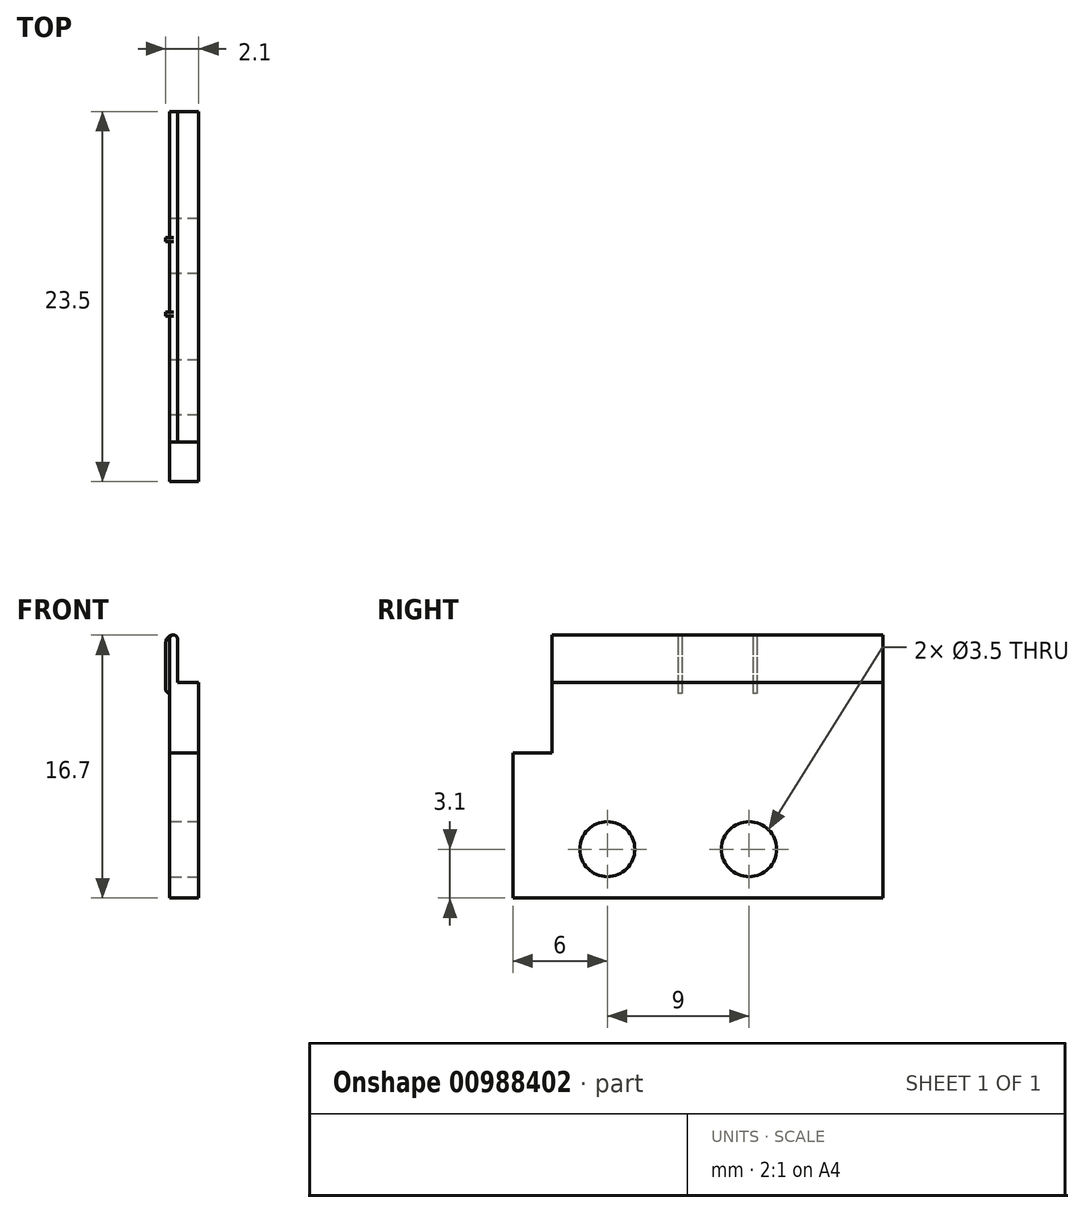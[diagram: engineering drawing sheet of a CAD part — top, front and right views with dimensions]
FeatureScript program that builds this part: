
annotation { "Feature Type Name" : "Feature", "Feature Type Description" : "" }
export const myFeature = defineFeature(function(context is Context, id is Id, definition is map)
    precondition{}
    {
        {
            var Q0;
            Q0=qCreatedBy(makeId("Right.planeOp"),FACE);
            var sketch = newSketch(context, id + "F0", { "sketchPlane" : qUnion([Q0])});
            skLineSegment(sketch, "E0", {"start": v(0, 0) * mm, "end": v(23.5, 0) * mm});
            skLineSegment(sketch, "E1", {"start": v(23.5, 0) * mm, "end": v(23.5, 13.7) * mm});
            skLineSegment(sketch, "E2", {"start": v(23.5, 13.7) * mm, "end": v(2.5, 13.7) * mm});
            skLineSegment(sketch, "E3", {"start": v(0, 0) * mm, "end": v(0, 9.2) * mm});
            skLineSegment(sketch, "E4", {"start": v(0, 9.2) * mm, "end": v(2.5, 9.2) * mm});
            skLineSegment(sketch, "E5", {"start": v(2.5, 13.7) * mm, "end": v(2.5, 9.2) * mm});
            skSolve(sketch);
        }
        {
            var Q0;
            Q0=makeQuery(id+"F0.imprint","IMPRINT",FACE,{"disambiguationData":[TD([[makeQuery(id+"F0.imprint","IMPRINT",EDGE,{"derivedFrom":sQuery(id+"F0.wireOp",EDGE,"E0")}),1.0]])]});
            extrude(context, id + "F1", {"entities" : qUnion([Q0]), "depth" : 1.85 * mm, "offsetDistance" : 25 * mm});
        }
        {
            var Q0;
            Q0=makeQuery(id+"F1.opExtrude","SWEPT_FACE",FACE,{"disambiguationData":[OSD([sQuery(id+"F0.wireOp",EDGE,"E2")])]});
            var sketch = newSketch(context, id + "F2", { "sketchPlane" : qUnion([Q0])});
            skLineSegment(sketch, "E6", {"start": v(0, 23.5) * mm, "end": v(0.5, 23.5) * mm});
            skLineSegment(sketch, "E7", {"start": v(0.5, 23.5) * mm, "end": v(0.5, 2.5) * mm});
            skLineSegment(sketch, "E8", {"start": v(0.5, 2.5) * mm, "end": v(0, 2.5) * mm});
            skLineSegment(sketch, "E9", {"start": v(0, 2.5) * mm, "end": v(0, 23.5) * mm});
            skSolve(sketch);
        }
        {
            var Q0;
            Q0=makeQuery(id+"F2.imprint","IMPRINT",FACE,{"disambiguationData":[TD([[makeQuery(id+"F2.imprint","IMPRINT",EDGE,{"derivedFrom":sQuery(id+"F2.wireOp",EDGE,"E6")}),1.0]])]});
            extrude(context, id + "F3", {"entities" : qUnion([Q0]), "operationType" : NewBodyOperationType.ADD, "depth" : 3 * mm, "offsetDistance" : 25 * mm});
        }
        {
            var Q0;
            Q0=makeQuery(id+"F1.opExtrude","CAP_FACE",FACE,{"disambiguationData":[OSD([sQuery(id+"F0.wireOp",EDGE,"E0"),sQuery(id+"F0.wireOp",EDGE,"E1"),sQuery(id+"F0.wireOp",EDGE,"E2"),sQuery(id+"F0.wireOp",EDGE,"E3"),sQuery(id+"F0.wireOp",EDGE,"E4"),sQuery(id+"F0.wireOp",EDGE,"E5")])],"isStart":false});
            var sketch = newSketch(context, id + "F4", { "sketchPlane" : qUnion([Q0])});
            skCircle(sketch, "E10", {"center": v(6, 3.1) * mm, "radius": 1.75 * mm});
            skCircle(sketch, "E11", {"center": v(15, 3.1) * mm, "radius": 1.75 * mm});
            skSolve(sketch);
        }
        {
            var Q0;
            Q0=makeQuery(id+"F4.imprint","IMPRINT",FACE,{"disambiguationData":[TD([[makeQuery(id+"F4.imprint","IMPRINT",EDGE,{"derivedFrom":sQuery(id+"F4.wireOp",EDGE,"E10")}),1.0]])]});
            var Q1;
            Q1=makeQuery(id+"F4.imprint","IMPRINT",FACE,{"disambiguationData":[TD([[makeQuery(id+"F4.imprint","IMPRINT",EDGE,{"derivedFrom":sQuery(id+"F4.wireOp",EDGE,"E11")}),1.0]])]});
            extrude(context, id + "F5", {"entities" : qUnion([Q0, Q1]), "operationType" : NewBodyOperationType.REMOVE, "endBound" : BoundingType.THROUGH_ALL, "oppositeDirection" : true, "depth" : 25 * mm, "offsetDistance" : 25 * mm});
        }
        {
            var Q0;
            Q0=makeQuery(id+"F3.boolean.opBoolean","MERGE",FACE,{"derivedFrom":[makeQuery(id+"F1.opExtrude","CAP_FACE",FACE,{"disambiguationData":[OSD([sQuery(id+"F0.wireOp",EDGE,"E0"),sQuery(id+"F0.wireOp",EDGE,"E1"),sQuery(id+"F0.wireOp",EDGE,"E2"),sQuery(id+"F0.wireOp",EDGE,"E3"),sQuery(id+"F0.wireOp",EDGE,"E4"),sQuery(id+"F0.wireOp",EDGE,"E5")])],"isStart":true}),makeQuery(id+"F3.opExtrude","SWEPT_FACE",FACE,{"disambiguationData":[OSD([sQuery(id+"F2.wireOp",EDGE,"E9")])]})]});
            var sketch = newSketch(context, id + "F6", { "sketchPlane" : qUnion([Q0])});
            skLineSegment(sketch, "E12", {"start": v(-10.75, 16.7) * mm, "end": v(-10.5, 16.7) * mm});
            skLineSegment(sketch, "E13", {"start": v(-15.25, 16.7) * mm, "end": v(-15.5, 16.7) * mm});
            skLineSegment(sketch, "E14", {"start": v(-10.5, 16.7) * mm, "end": v(-10.5, 13) * mm});
            skLineSegment(sketch, "E15", {"start": v(-10.75, 16.7) * mm, "end": v(-10.75, 13) * mm});
            skLineSegment(sketch, "E16", {"start": v(-10.75, 13) * mm, "end": v(-10.5, 13) * mm});
            skLineSegment(sketch, "E17", {"start": v(-15.25, 16.7) * mm, "end": v(-15.25, 13) * mm});
            skLineSegment(sketch, "E18", {"start": v(-15.5, 16.7) * mm, "end": v(-15.5, 13) * mm});
            skLineSegment(sketch, "E19", {"start": v(-15.5, 13) * mm, "end": v(-15.25, 13) * mm});
            skSolve(sketch);
        }
        {
            var Q0;
            Q0=makeQuery(id+"F6.imprint","IMPRINT",FACE,{"disambiguationData":[TD([[makeQuery(id+"F6.imprint","IMPRINT",EDGE,{"derivedFrom":sQuery(id+"F6.wireOp",EDGE,"E13")}),-1.0]])]});
            var Q1;
            Q1=makeQuery(id+"F6.imprint","IMPRINT",FACE,{"disambiguationData":[TD([[makeQuery(id+"F6.imprint","IMPRINT",EDGE,{"derivedFrom":sQuery(id+"F6.wireOp",EDGE,"E12")}),-1.0]])]});
            extrude(context, id + "F7", {"entities" : qUnion([Q0, Q1]), "operationType" : NewBodyOperationType.ADD, "depth" : 0.25 * mm, "offsetDistance" : 25 * mm});
        }
        {
            var Q0;
            {var subQ0=sQuery(id+"F2.wireOp",EDGE,"E9");var subQ2=sQuery(id+"F0.wireOp",EDGE,"E5");Q0=makeQuery(id+"F7.boolean.opBoolean","SPLIT",EDGE,{"disambiguationData":[TD([makeQuery(id+"F1.opExtrude","SWEPT_FACE",FACE,{"disambiguationData":[OSD([subQ2])]})])],"derivedFrom":makeQuery(id+"F3.opExtrude","CAP_EDGE",EDGE,{"disambiguationData":[OSD([subQ0])],"isStart":false})});}
            var Q1;
            {var subQ0=sQuery(id+"F2.wireOp",EDGE,"E9");Q1=makeQuery(id+"F7.boolean.opBoolean","SPLIT",EDGE,{"disambiguationData":[TD([makeQuery(id+"F7.opExtrude","SWEPT_FACE",FACE,{"disambiguationData":[OSD([sQuery(id+"F6.wireOp",EDGE,"E15")])]})])],"derivedFrom":makeQuery(id+"F3.opExtrude","CAP_EDGE",EDGE,{"disambiguationData":[OSD([subQ0])],"isStart":false})});}
            var Q2;
            {var subQ0=sQuery(id+"F2.wireOp",EDGE,"E9");var subQ2=sQuery(id+"F0.wireOp",EDGE,"E1");Q2=makeQuery(id+"F7.boolean.opBoolean","SPLIT",EDGE,{"disambiguationData":[TD([makeQuery(id+"F1.opExtrude","SWEPT_FACE",FACE,{"disambiguationData":[OSD([subQ2])]})])],"derivedFrom":makeQuery(id+"F3.opExtrude","CAP_EDGE",EDGE,{"disambiguationData":[OSD([subQ0])],"isStart":false})});}
            var Q3;
            Q3=makeQuery(id+"F3.opExtrude","CAP_EDGE",EDGE,{"disambiguationData":[OSD([sQuery(id+"F2.wireOp",EDGE,"E7")])],"isStart":false});
            fillet(context, id + "F8", {"entities" : qUnion([Q0, Q1, Q2, Q3]), "radius" : 0.25 * mm, "tangentPropagation" : true, "allowEdgeOverflow" : false});
        }
        {
            var Q0;
            Q0=makeQuery(id+"F7.opExtrude","CAP_EDGE",EDGE,{"disambiguationData":[OSD([sQuery(id+"F6.wireOp",EDGE,"E13")])],"isStart":false});
            var Q1;
            Q1=makeQuery(id+"F7.opExtrude","CAP_EDGE",EDGE,{"disambiguationData":[OSD([sQuery(id+"F6.wireOp",EDGE,"E12")])],"isStart":false});
            fillet(context, id + "F9", {"entities" : qUnion([Q0, Q1]), "radius" : 0.5 * mm, "tangentPropagation" : true, "allowEdgeOverflow" : false});
        }
        {
            var Q0;
            Q0=makeQuery(id+"F7.opExtrude","CAP_EDGE",EDGE,{"disambiguationData":[OSD([sQuery(id+"F6.wireOp",EDGE,"E16")])],"isStart":false});
            var Q1;
            Q1=makeQuery(id+"F7.opExtrude","CAP_EDGE",EDGE,{"disambiguationData":[OSD([sQuery(id+"F6.wireOp",EDGE,"E19")])],"isStart":false});
            fillet(context, id + "F10", {"entities" : qUnion([Q0, Q1]), "radius" : 0.25 * mm, "tangentPropagation" : true, "allowEdgeOverflow" : false});
        }
    });
